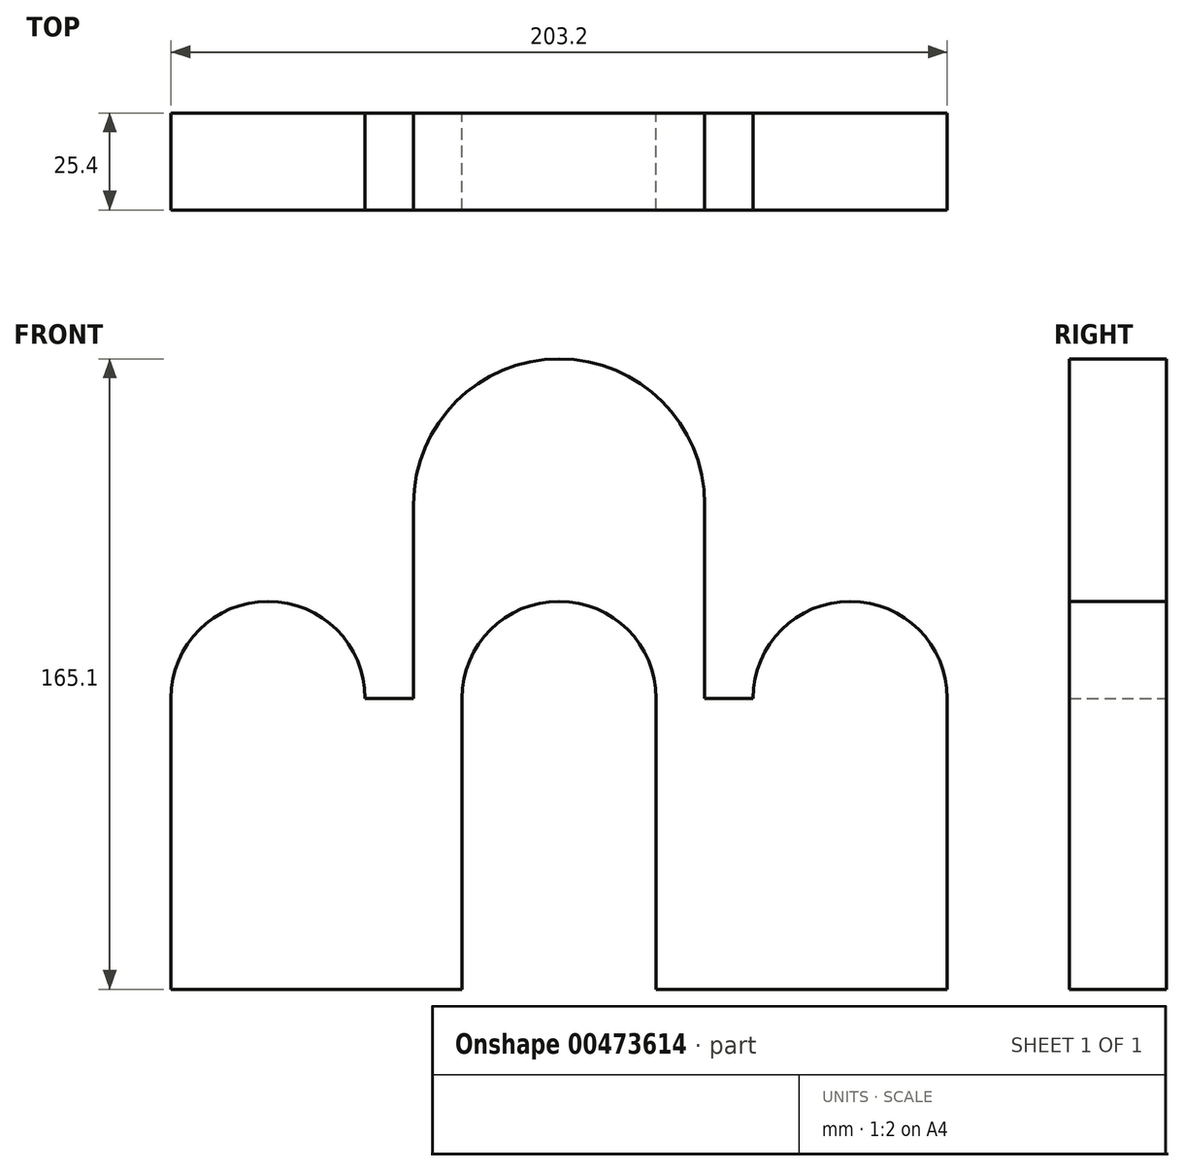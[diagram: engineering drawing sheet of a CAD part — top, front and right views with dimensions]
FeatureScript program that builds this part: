
annotation { "Feature Type Name" : "Feature", "Feature Type Description" : "" }
export const myFeature = defineFeature(function(context is Context, id is Id, definition is map)
    precondition{}
    {
        {
            var Q0;
            Q0=qCreatedBy(makeId("Front.planeOp"),FACE);
            var sketch = newSketch(context, id + "F0", { "sketchPlane" : qUnion([Q0])});
            skLineSegment(sketch, "E0", {"start": v(-40.74, -42.18) * mm, "end": v(35.46, -42.18) * mm});
            skLineSegment(sketch, "E1", {"start": v(35.46, -42.18) * mm, "end": v(35.46, 34.02) * mm});
            skLineSegment(sketch, "E2", {"start": v(-40.74, -42.18) * mm, "end": v(-40.74, 34.02) * mm});
            skArc(sketch, "E3", {"start": v(-40.74, 34.02) * mm, "mid": v(-15.34, 59.42) * mm, "end": v(10.06, 34.02) * mm});
            skLineSegment(sketch, "E4", {"start": v(-40.74, 34.02) * mm, "end": v(10.06, 34.02) * mm, "construction": true});
            skArc(sketch, "E5", {"start": v(35.46, 34.02) * mm, "mid": v(42.9, 51.98) * mm, "end": v(60.86, 59.42) * mm});
            skLineSegment(sketch, "E6", {"start": v(60.86, 34.02) * mm, "end": v(60.86, 75.99) * mm, "construction": true});
            skLineSegment(sketch, "E7", {"start": v(10.06, 34.02) * mm, "end": v(22.76, 34.02) * mm});
            skLineSegment(sketch, "E8", {"start": v(22.76, 34.02) * mm, "end": v(22.76, 84.82) * mm});
            skArc(sketch, "E9", {"start": v(22.76, 84.82) * mm, "mid": v(33.92, 111.76) * mm, "end": v(60.86, 122.92) * mm});
            skArc(sketch, "E10.MirrorCS", {"start": v(98.96, 84.82) * mm, "mid": v(87.8, 111.76) * mm, "end": v(60.86, 122.92) * mm});
            skLineSegment(sketch, "E11.MirrorCS", {"start": v(98.96, 34.02) * mm, "end": v(98.96, 84.82) * mm});
            skArc(sketch, "E12.MirrorCS", {"start": v(162.46, 34.02) * mm, "mid": v(137.06, 59.42) * mm, "end": v(111.66, 34.02) * mm});
            skLineSegment(sketch, "E13.MirrorCS", {"start": v(111.66, 34.02) * mm, "end": v(98.96, 34.02) * mm});
            skLineSegment(sketch, "E14.MirrorCS", {"start": v(162.46, -42.18) * mm, "end": v(162.46, 34.02) * mm});
            skLineSegment(sketch, "E15.MirrorCS", {"start": v(86.26, -42.18) * mm, "end": v(86.26, 34.02) * mm});
            skLineSegment(sketch, "E16.MirrorCS", {"start": v(162.46, -42.18) * mm, "end": v(86.26, -42.18) * mm});
            skArc(sketch, "E17.MirrorCS", {"start": v(86.26, 34.02) * mm, "mid": v(78.82, 51.98) * mm, "end": v(60.86, 59.42) * mm});
            skSolve(sketch);
        }
        {
            var Q0;
            Q0 = qSketchRegion(id + "F0", true);
            extrude(context, id + "F1", {"entities" : qUnion([Q0]), "depth" : 25.4 * mm});
        }
    });
